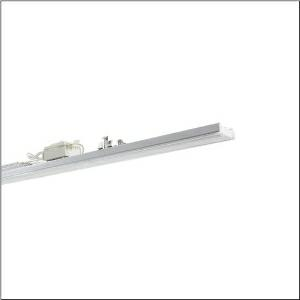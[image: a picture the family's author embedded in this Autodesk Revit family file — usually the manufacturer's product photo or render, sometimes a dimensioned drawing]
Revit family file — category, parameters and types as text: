
# Revit family: licross_21_recessed_mo_52tl12dn455g
name_source: partatom
category: Lighting Fixtures
units: mm (PartAtom-declared; Revit-internal decimal feet)

## family parameters
Cut with Voids When Loaded = No
Host = Face
Light Source = No
Part Type = Normal
Room Calculation Point = No
Round Connector Dimension = Use Diameter
Shared = No

## types (1)
- --- (1 x LED, 5500 lm, 29.6 W, 4000K)
    Apparent Load = 30 VA
    CIE Flux Codes = 72 92 99 100 100
    Color Rendering = 80
    Color Temperature = 4000K
    Default Elevation = 1800 mm
    Description = Licross 21 Recessed MO, luminaire insert, of sheet steel, galvanised, coil coated, white, length: 1.500mm, width: 66mm, height: 67mm, LED rated luminous flux: 5.500lm, light colour: 840, SDCM (Standard Deviation of Colour Matching)MacAdam ≤ 3 SDCM (initial), control gear: DALI 2, with plug, 5-pole, with phase selection, mains connection: 220..240V, AC, 50/60Hz, rated input power: 30W, internal wiring halogen-free, primary optical cover: cover, of PMMA, light emission: direct distribution, primary light characteristic: symmetric, protection rating (complete): IP40, insulation class (complete): insulation class I (protective earthing), certification: CE, ENEC, VDE, UKCA, protection symbol: D if used in an environment without relevant dust loads with corresponding accessories, impact resistance: IK06, permissible ambient temperature for indoor applications: -25..+45°C, corresponds to IFS (International Featured Standards) requirements for safety and quality in the food industry, reducing of maximum allowable ambient temperature of 5°C with ceiling mounting, LABS conformity tested according to VDMA 24364:2018-05, The light source and the operating device comply with the requirements of the Ecodesign Regulation (EU) 2019/2020 and are replaceable in accordance with this regulation, packaging unit: 1 piece
    Height = 58 mm
    Lamp = 1 x LED
    Lamp Light Flux = 5500 lm
    Lamp Power = 29.6 W
    Lamp count = 1
    Length = 1500 mm
    Luminous efficacy = 186 lm/W
    Manufacturer = Siteco
    ModVariant = No
    Model = 52TL12DN455G
    Mounting Place = Ceiling
    Mounting Type = Pendant
    Number of Poles = 1
    OnlyDefault = Yes
    Power Factor = 1
    Product Name = Licross 21 Recessed MO
    Product group = luminaire insert | ceiling pendant
    ProductGroupID = 901
    Protection Class = Protection class I
    Protection Degree = IP 40
    RLX_Detail_Level = 1
    RLX_Emergency_Light_Flux = 0 lm
    RLX_Emergency_Type = 0
    RLX_Emergency_Type_DB = No
    RlxData = <blob elided: 24297 chars, md5=6cd8ff14>
    Socket = socket
    Standby Power = 0 W
    System Light Flux = 5500 lm
    System Power = 30 W
    Type Comments = factory setting: luminous flux: 100 % | dim-lin: 254 | 200 mA
    Type Image = l_1296930.jpg
    URL = http://relux.com
    VarID = @adj_126421
    Voltage = 0 V
    Weight = 0.00 kg
    Width = 66 mm

## geometry (parser evidence)
native form markers: Blend x4, Sweep x12
no freeform markers — native parametric forms only
